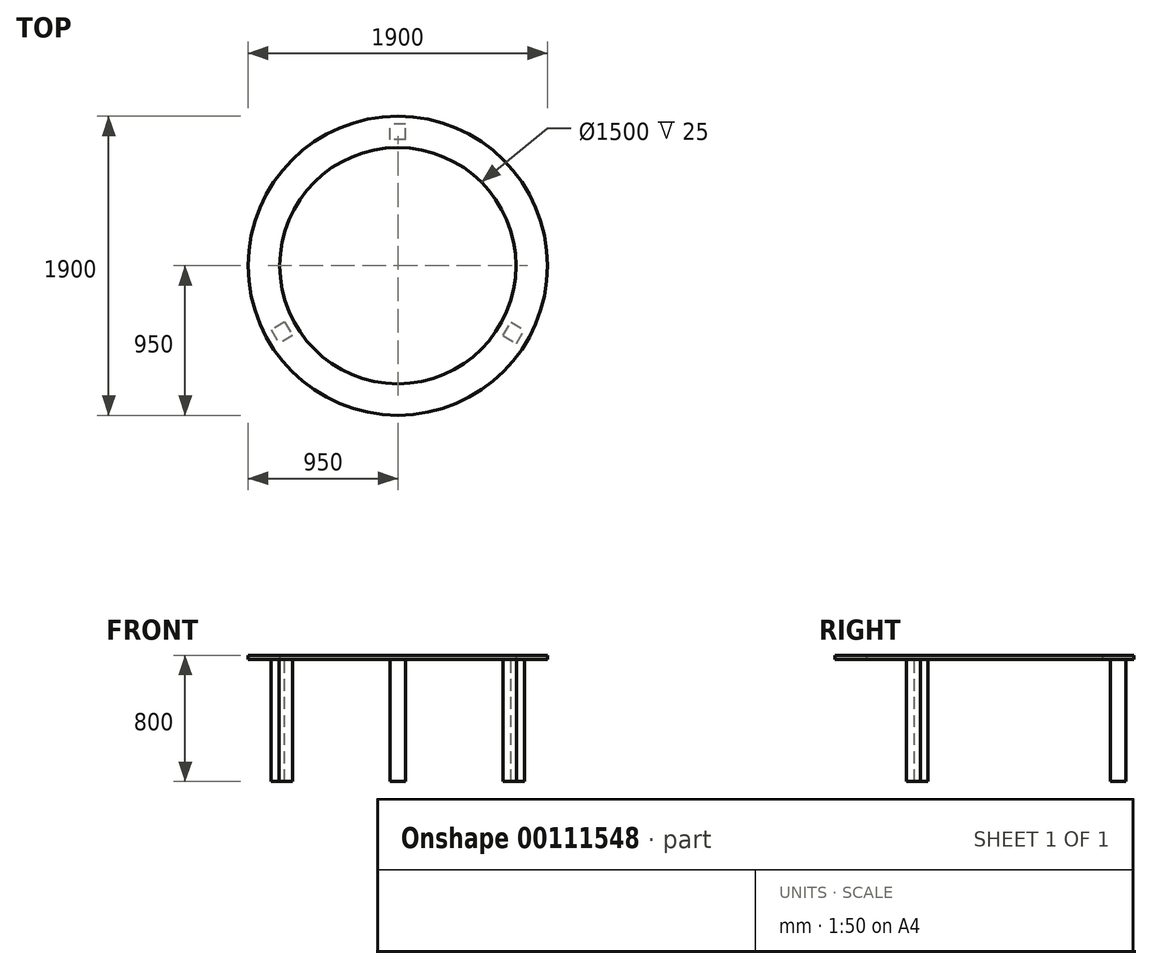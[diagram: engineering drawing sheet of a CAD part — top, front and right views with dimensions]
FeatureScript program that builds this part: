
annotation { "Feature Type Name" : "Feature", "Feature Type Description" : "" }
export const myFeature = defineFeature(function(context is Context, id is Id, definition is map)
    precondition{}
    {
        {
            var Q0;
            Q0=qCreatedBy(makeId("Top.planeOp"),FACE);
            var sketch = newSketch(context, id + "F0", { "sketchPlane" : qUnion([Q0])});
            skCircle(sketch, "E0", {"center": v(0, 0) * mm, "radius": 750 * mm});
            skCircle(sketch, "E1", {"center": v(0, 0) * mm, "radius": 950 * mm});
            skSolve(sketch);
        }
        {
            var Q0;
            Q0 = qSketchRegion(id + "F0", true);
            extrude(context, id + "F1", {"entities" : qUnion([Q0]), "depth" : 25 * mm});
        }
        {
            var Q0;
            Q0=makeQuery(id+"F1.opExtrude","CAP_FACE",FACE,{"disambiguationData":[OSD([sQuery(id+"F0.wireOp",EDGE,"E0"),sQuery(id+"F0.wireOp",EDGE,"E1")])],"isStart":true});
            var sketch = newSketch(context, id + "F2", { "sketchPlane" : qUnion([Q0])});
            skLineSegment(sketch, "E2.bottom", {"start": v(50, -800) * mm, "end": v(-50, -800) * mm});
            skLineSegment(sketch, "E2.top", {"start": v(50, -900) * mm, "end": v(-50, -900) * mm});
            skLineSegment(sketch, "E2.left", {"start": v(50, -800) * mm, "end": v(50, -900) * mm});
            skLineSegment(sketch, "E2.right", {"start": v(-50, -800) * mm, "end": v(-50, -900) * mm});
            skPoint(sketch, "E2.middle", {"position": v(0, -850) * mm});
            skLineSegment(sketch, "E3", {"start": v(0, -750) * mm, "end": v(0, -950) * mm, "construction": true});
            skLineSegment(sketch, "E4.1.0", {"start": v(-649.52, 375) * mm, "end": v(-822.72, 475) * mm, "construction": true});
            skLineSegment(sketch, "E4.1.1", {"start": v(-667.82, 443.3) * mm, "end": v(-754.42, 493.3) * mm});
            skLineSegment(sketch, "E4.1.2", {"start": v(-717.82, 356.7) * mm, "end": v(-804.42, 406.7) * mm});
            skLineSegment(sketch, "E4.1.3", {"start": v(-804.42, 406.7) * mm, "end": v(-754.42, 493.3) * mm});
            skLineSegment(sketch, "E4.1.4", {"start": v(-717.82, 356.7) * mm, "end": v(-667.82, 443.3) * mm});
            skPoint(sketch, "E4.1.5", {"position": v(-736.12, 425) * mm});
            skLineSegment(sketch, "E4.2.0", {"start": v(649.52, 375) * mm, "end": v(822.72, 475) * mm, "construction": true});
            skLineSegment(sketch, "E4.2.1", {"start": v(717.82, 356.7) * mm, "end": v(804.42, 406.7) * mm});
            skLineSegment(sketch, "E4.2.2", {"start": v(667.82, 443.3) * mm, "end": v(754.42, 493.3) * mm});
            skLineSegment(sketch, "E4.2.3", {"start": v(754.42, 493.3) * mm, "end": v(804.42, 406.7) * mm});
            skLineSegment(sketch, "E4.2.4", {"start": v(667.82, 443.3) * mm, "end": v(717.82, 356.7) * mm});
            skPoint(sketch, "E4.2.5", {"position": v(736.12, 425) * mm});
            skPoint(sketch, "E4.center", {"position": v(0, 0) * mm});
            skLineSegment(sketch, "E4.anchor1", {"start": v(0, 0) * mm, "end": v(0, -950) * mm, "construction": true});
            skLineSegment(sketch, "E4.anchor2", {"start": v(0, 0) * mm, "end": v(822.72, 475) * mm, "construction": true});
            skSolve(sketch);
        }
        {
            var Q0;
            Q0 = qSketchRegion(id + "F2", true);
            extrude(context, id + "F3", {"entities" : qUnion([Q0]), "operationType" : NewBodyOperationType.ADD, "depth" : 775 * mm});
        }
    });
